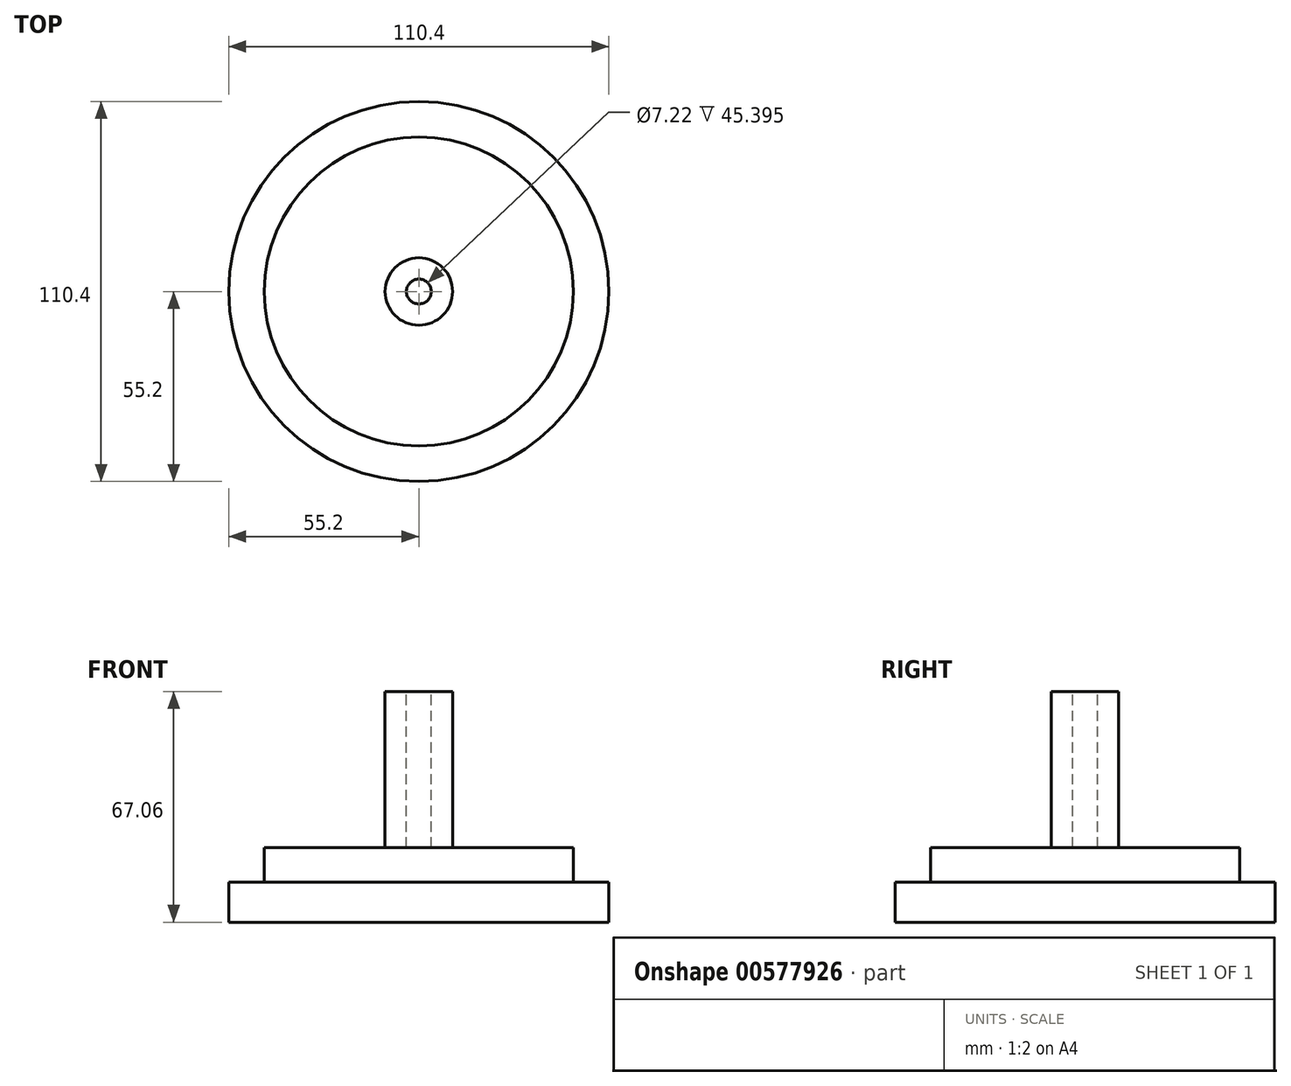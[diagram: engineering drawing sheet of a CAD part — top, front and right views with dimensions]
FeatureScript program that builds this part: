
annotation { "Feature Type Name" : "Feature", "Feature Type Description" : "" }
export const myFeature = defineFeature(function(context is Context, id is Id, definition is map)
    precondition{}
    {
        {
            var Q0;
            Q0=qCreatedBy(makeId("Right.planeOp"),FACE);
            var sketch = newSketch(context, id + "F0", { "sketchPlane" : qUnion([Q0])});
            skLineSegment(sketch, "E0", {"start": v(0, -11.6) * mm, "end": v(55.2, -11.6) * mm});
            skLineSegment(sketch, "E1", {"start": v(55.2, -11.6) * mm, "end": v(55.2, 0) * mm});
            skLineSegment(sketch, "E2", {"start": v(55.2, 0) * mm, "end": v(44.88, 0) * mm});
            skLineSegment(sketch, "E3", {"start": v(44.88, 0) * mm, "end": v(44.88, 10.06) * mm});
            skLineSegment(sketch, "E4", {"start": v(44.88, 10.06) * mm, "end": v(9.8, 10.06) * mm});
            skLineSegment(sketch, "E5", {"start": v(9.8, 10.06) * mm, "end": v(9.8, 55.45) * mm});
            skLineSegment(sketch, "E6", {"start": v(9.8, 55.45) * mm, "end": v(3.61, 55.45) * mm});
            skLineSegment(sketch, "E7", {"start": v(3.61, 55.45) * mm, "end": v(3.61, 10.06) * mm});
            skLineSegment(sketch, "E8", {"start": v(3.61, 10.06) * mm, "end": v(0, 10.06) * mm});
            skLineSegment(sketch, "E9", {"start": v(0, 10.06) * mm, "end": v(0, -11.6) * mm});
            skSolve(sketch);
        }
        {
            var Q0;
            Q0 = qSketchRegion(id + "F0", true);
            var Q1;
            Q1=sQuery(id+"F0.wireOp",EDGE,"E9");
            revolve(context, id + "F1", {"entities" : qUnion([Q0]), "axis" : qUnion([Q1]), "revolveType" : RevolveType.FULL});
        }
    });
